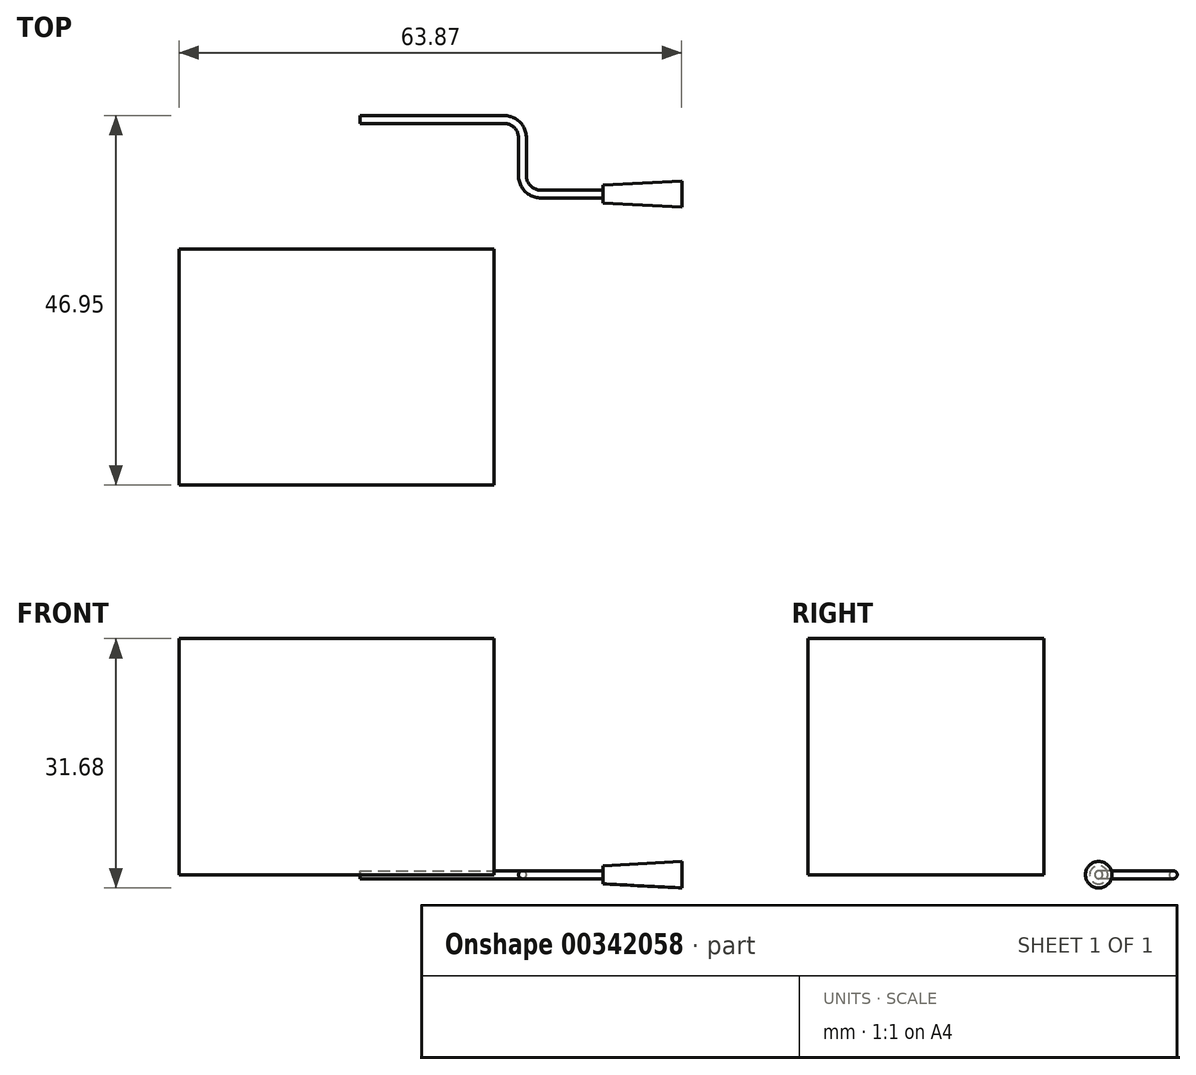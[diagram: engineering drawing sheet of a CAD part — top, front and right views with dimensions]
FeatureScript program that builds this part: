
annotation { "Feature Type Name" : "Feature", "Feature Type Description" : "" }
export const myFeature = defineFeature(function(context is Context, id is Id, definition is map)
    precondition{}
    {
        {
            var Q0;
            Q0=qCreatedBy(makeId("Top.planeOp"),FACE);
            var sketch = newSketch(context, id + "F0", { "sketchPlane" : qUnion([Q0])});
            skLineSegment(sketch, "E0.bottom", {"start": v(-23, -1.39) * mm, "end": v(17, -1.39) * mm});
            skLineSegment(sketch, "E0.top", {"start": v(-23, -31.39) * mm, "end": v(17, -31.39) * mm});
            skLineSegment(sketch, "E0.left", {"start": v(-23, -1.39) * mm, "end": v(-23, -31.39) * mm});
            skLineSegment(sketch, "E0.right", {"start": v(17, -1.39) * mm, "end": v(17, -31.39) * mm});
            skSolve(sketch);
        }
        {
            var Q0;
            Q0 = qSketchRegion(id + "F0", true);
            extrude(context, id + "F1", {"entities" : qUnion([Q0]), "depth" : 30 * mm});
        }
        {
            var Q0;
            Q0=qCreatedBy(makeId("Top.planeOp"),FACE);
            var sketch = newSketch(context, id + "F2", { "sketchPlane" : qUnion([Q0])});
            skLineSegment(sketch, "E1", {"start": v(0, 15.06) * mm, "end": v(18.3, 15.06) * mm});
            skArc(sketch, "E2", {"start": v(18.3, 15.06) * mm, "mid": v(19.96, 14.37) * mm, "end": v(20.65, 12.72) * mm});
            skLineSegment(sketch, "E3", {"start": v(20.65, 12.72) * mm, "end": v(20.65, 7.94) * mm});
            skArc(sketch, "E4", {"start": v(20.65, 7.94) * mm, "mid": v(21.34, 6.27) * mm, "end": v(23.01, 5.58) * mm});
            skLineSegment(sketch, "E5", {"start": v(23.01, 5.58) * mm, "end": v(30.88, 5.58) * mm});
            skSolve(sketch);
        }
        {
            var Q0;
            Q0=qCreatedBy(makeId("Right.planeOp"),FACE);
            var sketch = newSketch(context, id + "F3", { "sketchPlane" : qUnion([Q0])});
            skPoint(sketch, "E6.0", {"position": v(15.06, 0) * mm});
            skCircle(sketch, "E7", {"center": v(15.06, 0) * mm, "radius": 0.5 * mm});
            skSolve(sketch);
        }
        {
            var Q0;
            Q0=makeQuery(id+"F3.imprint","IMPRINT",FACE,{"disambiguationData":[TD([[makeQuery(id+"F3.imprint","IMPRINT",EDGE,{"derivedFrom":sQuery(id+"F3.wireOp",EDGE,"E7")}),1.0]])]});
            var Q1;
            Q1=sQuery(id+"F2.wireOp",EDGE,"E1");
            var Q2;
            Q2=sQuery(id+"F2.wireOp",EDGE,"E2");
            var Q3;
            Q3=sQuery(id+"F2.wireOp",EDGE,"E3");
            var Q4;
            Q4=sQuery(id+"F2.wireOp",EDGE,"E4");
            var Q5;
            Q5=sQuery(id+"F2.wireOp",EDGE,"E5");
            sweep(context, id + "F4", {"profiles" : qUnion([Q0]), "path" : qUnion([Q1, Q2, Q3, Q4, Q5])});
        }
        {
            var Q0;
            Q0=makeQuery(id+"F4.opSweep","CAP_FACE",FACE,{"disambiguationData":[OSD([sQuery(id+"F2.wireOp",VERTEX,"E5.end"),sQuery(id+"F3.wireOp",EDGE,"E7")])],"isStart":false});
            var sketch = newSketch(context, id + "F5", { "sketchPlane" : qUnion([Q0])});
            skCircle(sketch, "E8", {"center": v(5.58, 0) * mm, "radius": 1.16 * mm});
            skSolve(sketch);
        }
        {
            var Q0;
            Q0 = qSketchRegion(id + "F5", true);
            extrude(context, id + "F6", {"entities" : qUnion([Q0]), "operationType" : NewBodyOperationType.ADD, "depth" : 10 * mm, "hasDraft" : true, "draftAngle" : 3 * degree});
        }
    });
